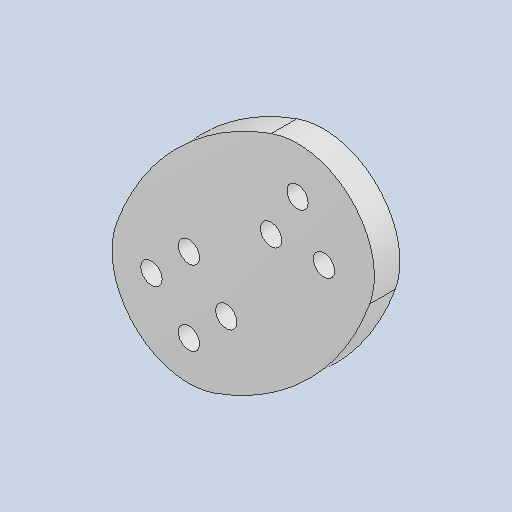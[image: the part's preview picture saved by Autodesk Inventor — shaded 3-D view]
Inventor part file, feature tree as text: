
AUTODESK INVENTOR PART (.ipt)
format: ipt  version: 2023 (Build 270158030, 158C)  size: 157,184 bytes
history: native  units: mm
features: other x4, sketch x2
ambient origin geometry x8: Origin, YZ Plane, XZ Plane, XY Plane, X Axis, Y Axis, Z Axis, Center Point
bodies: Solid2 (feature_tree)
feature tree (6):
  other  "駆動節.ipt"
  other  "Solid2::駆動節.ipt"
  other  "TaggingFeature1"
  sketch  "Sketch2"  dims[d0=10.0mm]
  sketch  "Sketch3"
  other  "sesaku"
